# Revit family: Go mirror cabinet 450
name_source: partatom
category: Furniture
units: mm (PartAtom-declared; Revit-internal decimal feet)

## family parameters
Always vertical = Yes
Cut with Voids When Loaded = No
OmniClass Number = 23.40.20.00
OmniClass Title = General Furniture and Specialties
Room Calculation Point = No
Shared = No
Work Plane-Based = No

## types (2) — shared parameters
Depth cabinet = 145 mm  [stored 0.475722 ft]
Glass doors = Mirror glass
Manufacturer = Hafa Bathroom Group AB
Material body = MDF/HDF/Chip board moisture restistant. E1 and FSC certified.
Model = Go mirror cabinets
URL = www.hafa.se
Width cabinet = 450 mm  [stored 1.47638 ft]

## per-type parameters (varying)
| type | Article number | Cabinet body | GTIN |
| Go mirror cabinet 450 white matt | 1580200 | NCS S 0300-N 20% gloss | 7330027103594 |
| Go mirror cabinet 450 black matt | 1580201 | NCS S 9000-N 10% gloss | 7330027103600 |

note: [stored X ft] marks values corroborated as IEEE doubles in the binary element streams (Revit-internal decimal feet)

## geometry (parser evidence)
native form markers: Sweep x2
no freeform markers — native parametric forms only
